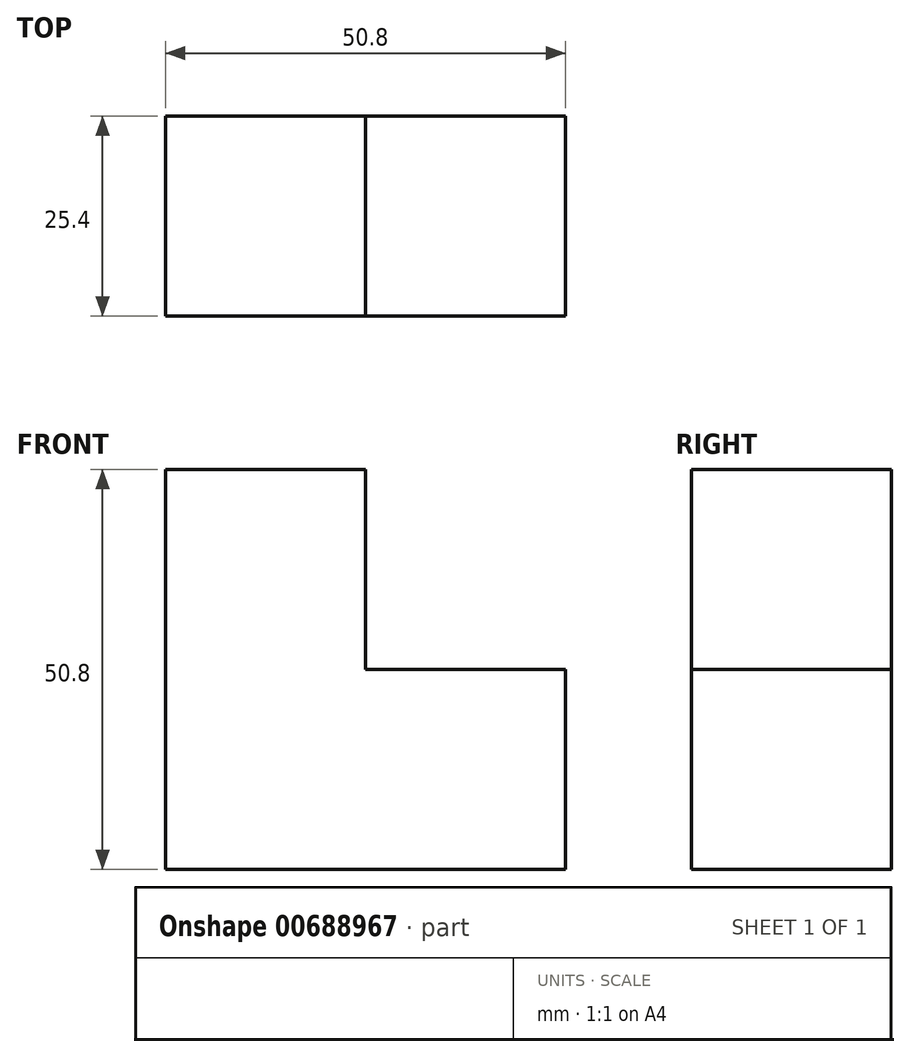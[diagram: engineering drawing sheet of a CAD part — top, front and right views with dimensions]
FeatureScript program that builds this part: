
annotation { "Feature Type Name" : "Feature", "Feature Type Description" : "" }
export const myFeature = defineFeature(function(context is Context, id is Id, definition is map)
    precondition{}
    {
        {
            var Q0;
            Q0=qCreatedBy(makeId("Front.planeOp"),FACE);
            var sketch = newSketch(context, id + "F0", { "sketchPlane" : qUnion([Q0])});
            skLineSegment(sketch, "E0", {"start": v(-46.5, 60.06) * mm, "end": v(-46.5, 9.26) * mm});
            skLineSegment(sketch, "E1", {"start": v(-46.5, 9.26) * mm, "end": v(4.3, 9.26) * mm});
            skLineSegment(sketch, "E2", {"start": v(4.3, 9.26) * mm, "end": v(4.3, 34.66) * mm});
            skLineSegment(sketch, "E3", {"start": v(4.3, 34.66) * mm, "end": v(-21.1, 34.66) * mm});
            skLineSegment(sketch, "E4", {"start": v(-21.1, 34.66) * mm, "end": v(-21.1, 60.06) * mm});
            skLineSegment(sketch, "E5", {"start": v(-21.1, 60.06) * mm, "end": v(-46.5, 60.06) * mm});
            skSolve(sketch);
        }
        {
            var Q0;
            Q0 = qSketchRegion(id + "F0", true);
            extrude(context, id + "F1", {"entities" : qUnion([Q0]), "depth" : 25.4 * mm, "offsetDistance" : 25.4 * mm});
        }
    });
